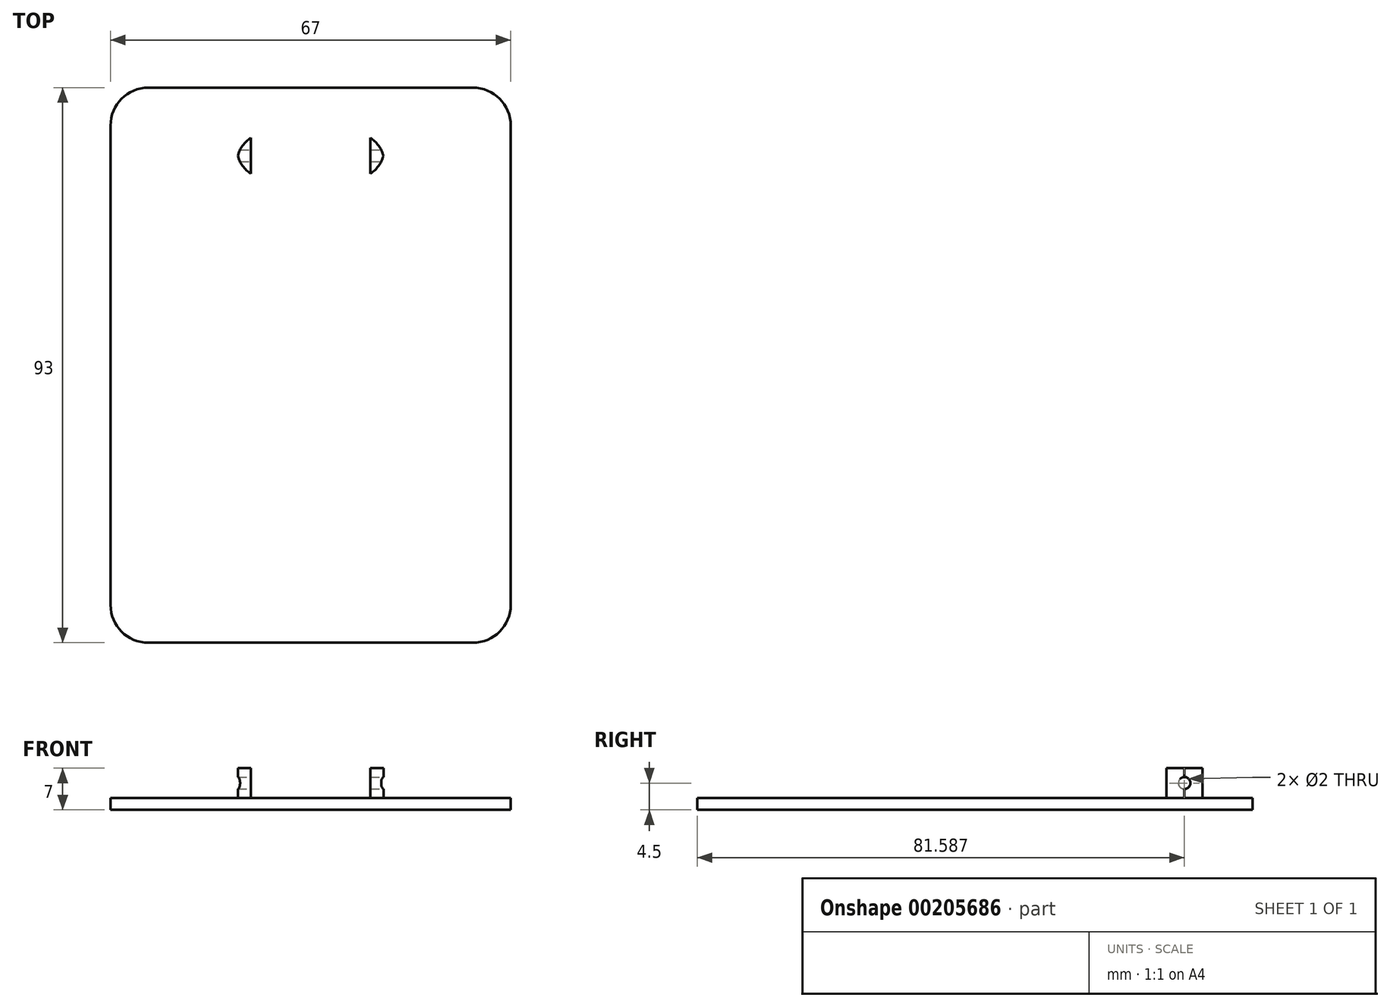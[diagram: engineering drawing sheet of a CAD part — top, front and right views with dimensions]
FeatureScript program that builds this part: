
annotation { "Feature Type Name" : "Feature", "Feature Type Description" : "" }
export const myFeature = defineFeature(function(context is Context, id is Id, definition is map)
    precondition{}
    {
        {
            var Q0;
            Q0=qCreatedBy(makeId("Top.planeOp"),FACE);
            var sketch = newSketch(context, id + "F0", { "sketchPlane" : qUnion([Q0])});
            skLineSegment(sketch, "E0.bottom", {"start": v(-27.15, 46.5) * mm, "end": v(27.15, 46.5) * mm});
            skLineSegment(sketch, "E0.top", {"start": v(-27.15, -46.5) * mm, "end": v(27.15, -46.5) * mm});
            skLineSegment(sketch, "E0.left", {"start": v(-33.5, 40.15) * mm, "end": v(-33.5, -40.15) * mm});
            skLineSegment(sketch, "E0.right", {"start": v(33.5, 40.15) * mm, "end": v(33.5, -40.15) * mm});
            skPoint(sketch, "E0.middle", {"position": v(0, 0) * mm});
            skPoint(sketch, "E1.visualSharp", {"position": v(-33.5, 46.5) * mm});
            skLineSegment(sketch, "E1.filletArc", {"start": v(-33.5, 46.5) * mm, "end": v(-33.5, 46.5) * mm});
            skPoint(sketch, "E2.visualSharp", {"position": v(33.5, 46.5) * mm});
            skLineSegment(sketch, "E2.filletArc", {"start": v(33.5, 46.5) * mm, "end": v(33.5, 46.5) * mm});
            skPoint(sketch, "E3.visualSharp", {"position": v(33.5, -46.5) * mm});
            skLineSegment(sketch, "E3.filletArc", {"start": v(33.5, -46.5) * mm, "end": v(33.5, -46.5) * mm});
            skPoint(sketch, "E4.visualSharp", {"position": v(-33.5, -46.5) * mm});
            skLineSegment(sketch, "E4.filletArc", {"start": v(-33.5, -46.5) * mm, "end": v(-33.5, -46.5) * mm});
            skPoint(sketch, "E5.middle", {"position": v(0, 25.08) * mm});
            skArc(sketch, "E6.filletArc", {"start": v(-33.5, -40.15) * mm, "mid": v(-31.64, -44.64) * mm, "end": v(-27.15, -46.5) * mm});
            skArc(sketch, "E7.filletArc", {"start": v(27.15, -46.5) * mm, "mid": v(31.64, -44.64) * mm, "end": v(33.5, -40.15) * mm});
            skArc(sketch, "E8.filletArc", {"start": v(-27.15, 46.5) * mm, "mid": v(-31.64, 44.64) * mm, "end": v(-33.5, 40.15) * mm});
            skArc(sketch, "E9.filletArc", {"start": v(33.5, 40.15) * mm, "mid": v(31.64, 44.64) * mm, "end": v(27.15, 46.5) * mm});
            skSolve(sketch);
        }
        {
            var Q0;
            Q0=makeQuery(id+"F0.imprint","IMPRINT",FACE,{"disambiguationData":[TD([[makeQuery(id+"F0.imprint","IMPRINT",EDGE,{"derivedFrom":sQuery(id+"F0.wireOp",EDGE,"E0.bottom")}),-1.0]])]});
            extrude(context, id + "F1", {"entities" : qUnion([Q0]), "depth" : 2 * mm});
        }
        {
            var Q0;
            Q0=makeQuery(id+"F1.opExtrude","CAP_FACE",FACE,{"disambiguationData":[OSD([sQuery(id+"F0.wireOp",EDGE,"E0.bottom"),sQuery(id+"F0.wireOp",EDGE,"E0.top"),sQuery(id+"F0.wireOp",EDGE,"E0.left"),sQuery(id+"F0.wireOp",EDGE,"E0.right"),sQuery(id+"F0.wireOp",EDGE,"E6.filletArc"),sQuery(id+"F0.wireOp",EDGE,"E7.filletArc"),sQuery(id+"F0.wireOp",EDGE,"E8.filletArc"),sQuery(id+"F0.wireOp",EDGE,"E9.filletArc")])],"isStart":false});
            var sketch = newSketch(context, id + "F2", { "sketchPlane" : qUnion([Q0])});
            skLineSegment(sketch, "E10", {"start": v(0, 35.09) * mm, "end": v(-10, 35.09) * mm});
            skLineSegment(sketch, "E11.MirrorCS", {"start": v(0, 35.09) * mm, "end": v(10, 35.09) * mm});
            skLineSegment(sketch, "E12.bottom", {"start": v(-10, 35.09) * mm, "end": v(-12.35, 35.09) * mm});
            skLineSegment(sketch, "E12.top", {"start": v(-10, 38.09) * mm, "end": v(-12.35, 38.09) * mm});
            skLineSegment(sketch, "E12.left", {"start": v(-10, 35.09) * mm, "end": v(-10, 38.09) * mm});
            skLineSegment(sketch, "E12.right", {"start": v(-12.35, 35.09) * mm, "end": v(-12.35, 38.09) * mm});
            skLineSegment(sketch, "E13.MirrorCS", {"start": v(-10, 35.09) * mm, "end": v(-10, 32.09) * mm});
            skLineSegment(sketch, "E14.MirrorCS", {"start": v(-12.35, 35.09) * mm, "end": v(-12.35, 32.09) * mm});
            skLineSegment(sketch, "E15.MirrorCS", {"start": v(-10, 32.09) * mm, "end": v(-12.35, 32.09) * mm});
            skLineSegment(sketch, "E16.MirrorCS", {"start": v(10, 35.09) * mm, "end": v(10, 38.09) * mm});
            skLineSegment(sketch, "E17.MirrorCS", {"start": v(12.35, 35.09) * mm, "end": v(12.35, 38.09) * mm});
            skLineSegment(sketch, "E18.MirrorCS", {"start": v(10, 38.09) * mm, "end": v(12.35, 38.09) * mm});
            skLineSegment(sketch, "E19.MirrorCS", {"start": v(10, 35.09) * mm, "end": v(10, 32.09) * mm});
            skLineSegment(sketch, "E20.MirrorCS", {"start": v(12.35, 35.09) * mm, "end": v(12.35, 32.09) * mm});
            skLineSegment(sketch, "E21.MirrorCS", {"start": v(10, 32.09) * mm, "end": v(12.35, 32.09) * mm});
            skLineSegment(sketch, "E22", {"start": v(-11.47, 35.09) * mm, "end": v(-11.47, 36.09) * mm});
            skLineSegment(sketch, "E23.MirrorCS", {"start": v(-11.47, 35.09) * mm, "end": v(-11.47, 34.09) * mm});
            skLineSegment(sketch, "E24.MirrorCS", {"start": v(11.47, 35.09) * mm, "end": v(11.47, 36.09) * mm});
            skLineSegment(sketch, "E25.MirrorCS", {"start": v(11.47, 35.09) * mm, "end": v(11.47, 34.09) * mm});
            skSolve(sketch);
        }
        {
            var Q0;
            Q0=makeQuery(id+"F2.imprint","IMPRINT",FACE,{"disambiguationData":[TD([[makeQuery(id+"F2.imprint","IMPRINT",EDGE,{"derivedFrom":sQuery(id+"F2.wireOp",EDGE,"E12.top")}),1.0]])]});
            var Q1;
            {var subQ3=sQuery(id+"F2.wireOp",EDGE,"E13.MirrorCS");Q1=makeQuery(id+"F2.imprint","IMPRINT",FACE,{"disambiguationData":[TD([[makeQuery(id+"F2.imprint","IMPRINT",EDGE,{"derivedFrom":subQ3}),-1.0]])]});}
            var Q2;
            Q2=makeQuery(id+"F2.imprint","IMPRINT",FACE,{"disambiguationData":[TD([[makeQuery(id+"F2.imprint","IMPRINT",EDGE,{"derivedFrom":sQuery(id+"F2.wireOp",EDGE,"E16.MirrorCS")}),-1.0]])]});
            extrude(context, id + "F3", {"entities" : qUnion([Q0, Q1, Q2]), "operationType" : NewBodyOperationType.ADD, "depth" : 5 * mm});
        }
        {
            var Q0;
            Q0=makeQuery(id+"F3.opExtrude","SWEPT_FACE",FACE,{"disambiguationData":[OSD([sQuery(id+"F2.wireOp",EDGE,"E12.right"),sQuery(id+"F2.wireOp",EDGE,"E14.MirrorCS")])]});
            var sketch = newSketch(context, id + "F4", { "sketchPlane" : qUnion([Q0])});
            skLineSegment(sketch, "E26", {"start": v(-35.09, 2) * mm, "end": v(-35.09, 4.5) * mm});
            skCircle(sketch, "E27", {"center": v(-35.09, 4.5) * mm, "radius": 1 * mm});
            skSolve(sketch);
        }
        {
            var Q0;
            Q0=makeQuery(id+"F3.opExtrude","SWEPT_FACE",FACE,{"disambiguationData":[OSD([sQuery(id+"F2.wireOp",EDGE,"E17.MirrorCS"),sQuery(id+"F2.wireOp",EDGE,"E20.MirrorCS")])]});
            var sketch = newSketch(context, id + "F5", { "sketchPlane" : qUnion([Q0])});
            skLineSegment(sketch, "E28", {"start": v(35.09, 2) * mm, "end": v(35.09, 4.5) * mm});
            skCircle(sketch, "E29", {"center": v(35.09, 4.5) * mm, "radius": 1 * mm});
            skSolve(sketch);
        }
        {
            var Q0;
            Q0=makeQuery(id+"F5.imprint","IMPRINT",FACE,{"disambiguationData":[TD([[makeQuery(id+"F5.imprint","IMPRINT",EDGE,{"derivedFrom":sQuery(id+"F5.wireOp",EDGE,"E29")}),1.0]])]});
            var Q1;
            Q1=makeQuery(id+"F4.imprint","IMPRINT",FACE,{"disambiguationData":[TD([[makeQuery(id+"F4.imprint","IMPRINT",EDGE,{"derivedFrom":sQuery(id+"F4.wireOp",EDGE,"E27")}),1.0]])]});
            extrude(context, id + "F6", {"entities" : qUnion([Q0, Q1]), "operationType" : NewBodyOperationType.REMOVE, "oppositeDirection" : true, "depth" : 25.4 * mm});
        }
        {
            var Q0;
            Q0=makeQuery(id+"F3.opExtrude","SWEPT_EDGE",EDGE,{"disambiguationData":[OSD([sQuery(id+"F2.wireOp",EDGE,"E14.MirrorCS"),sQuery(id+"F2.wireOp",EDGE,"E15.MirrorCS")])]});
            var Q1;
            Q1=makeQuery(id+"F3.opExtrude","SWEPT_EDGE",EDGE,{"disambiguationData":[OSD([sQuery(id+"F2.wireOp",EDGE,"E12.top"),sQuery(id+"F2.wireOp",EDGE,"E12.right")])]});
            var Q2;
            Q2=makeQuery(id+"F3.opExtrude","SWEPT_EDGE",EDGE,{"disambiguationData":[OSD([sQuery(id+"F2.wireOp",EDGE,"E20.MirrorCS"),sQuery(id+"F2.wireOp",EDGE,"E21.MirrorCS")])]});
            var Q3;
            Q3=makeQuery(id+"F3.opExtrude","SWEPT_EDGE",EDGE,{"disambiguationData":[OSD([sQuery(id+"F2.wireOp",EDGE,"E17.MirrorCS"),sQuery(id+"F2.wireOp",EDGE,"E18.MirrorCS")])]});
            fillet(context, id + "F7", {"entities" : qUnion([Q0, Q1, Q2, Q3]), "radius" : 5.08 * mm, "tangentPropagation" : true, "allowEdgeOverflow" : false});
        }
    });
